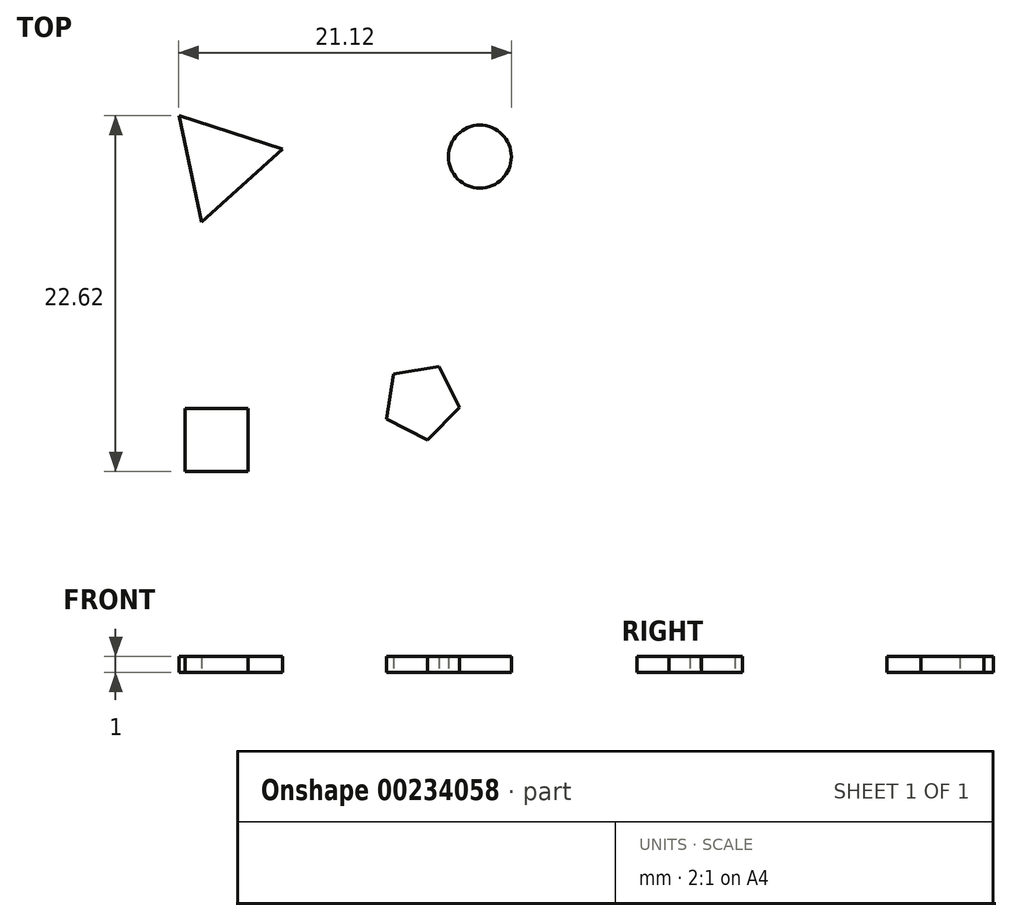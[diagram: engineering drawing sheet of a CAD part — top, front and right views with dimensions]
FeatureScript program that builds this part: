
annotation { "Feature Type Name" : "Feature", "Feature Type Description" : "" }
export const myFeature = defineFeature(function(context is Context, id is Id, definition is map)
    precondition{}
    {
        {
            var Q0;
            Q0=qCreatedBy(makeId("Top.planeOp"),FACE);
            var sketch = newSketch(context, id + "F0", { "sketchPlane" : qUnion([Q0])});
            skCircle(sketch, "E0.cCircle", {"center": v(-33.23, 10.22) * mm, "radius": 2 * mm, "construction": true});
            skLineSegment(sketch, "E0.0", {"start": v(-29.32, 11.06) * mm, "end": v(-34.46, 6.41) * mm});
            skLineSegment(sketch, "E0.1", {"start": v(-34.46, 6.41) * mm, "end": v(-35.92, 13.19) * mm});
            skLineSegment(sketch, "E0.2", {"start": v(-35.92, 13.19) * mm, "end": v(-29.32, 11.06) * mm});
            skPoint(sketch, "E0.0.midPoint", {"position": v(-31.9, 8.74) * mm});
            skCircle(sketch, "E1.cCircle", {"center": v(-33.51, -7.43) * mm, "radius": 2 * mm, "construction": true});
            skLineSegment(sketch, "E1.0", {"start": v(-31.51, -5.43) * mm, "end": v(-31.51, -9.43) * mm});
            skLineSegment(sketch, "E1.1", {"start": v(-31.51, -9.43) * mm, "end": v(-35.51, -9.43) * mm});
            skLineSegment(sketch, "E1.2", {"start": v(-35.51, -9.43) * mm, "end": v(-35.51, -5.43) * mm});
            skLineSegment(sketch, "E1.3", {"start": v(-35.51, -5.43) * mm, "end": v(-31.51, -5.43) * mm});
            skPoint(sketch, "E1.0.midPoint", {"position": v(-31.51, -7.43) * mm});
            skCircle(sketch, "E2.cCircle", {"center": v(-20.52, -4.96) * mm, "radius": 2 * mm, "construction": true});
            skLineSegment(sketch, "E2.0", {"start": v(-18.08, -5.35) * mm, "end": v(-20.13, -7.4) * mm});
            skLineSegment(sketch, "E2.1", {"start": v(-20.13, -7.4) * mm, "end": v(-22.72, -6.08) * mm});
            skLineSegment(sketch, "E2.2", {"start": v(-22.72, -6.08) * mm, "end": v(-22.27, -3.21) * mm});
            skLineSegment(sketch, "E2.3", {"start": v(-22.27, -3.21) * mm, "end": v(-19.4, -2.76) * mm});
            skLineSegment(sketch, "E2.4", {"start": v(-19.4, -2.76) * mm, "end": v(-18.08, -5.35) * mm});
            skPoint(sketch, "E2.0.midPoint", {"position": v(-19.1, -6.38) * mm});
            skCircle(sketch, "E3", {"center": v(-16.8, 10.58) * mm, "radius": 2 * mm});
            skSolve(sketch);
        }
        {
            var Q0;
            Q0=makeQuery(id+"F0.imprint","IMPRINT",FACE,{"disambiguationData":[TD([[makeQuery(id+"F0.imprint","IMPRINT",EDGE,{"derivedFrom":sQuery(id+"F0.wireOp",EDGE,"E0.0")}),-1.0]])]});
            var Q1;
            Q1=makeQuery(id+"F0.imprint","IMPRINT",FACE,{"disambiguationData":[TD([[makeQuery(id+"F0.imprint","IMPRINT",EDGE,{"derivedFrom":sQuery(id+"F0.wireOp",EDGE,"E1.0")}),-1.0]])]});
            var Q2;
            Q2=makeQuery(id+"F0.imprint","IMPRINT",FACE,{"disambiguationData":[TD([[makeQuery(id+"F0.imprint","IMPRINT",EDGE,{"derivedFrom":sQuery(id+"F0.wireOp",EDGE,"E2.0")}),-1.0]])]});
            var Q3;
            Q3=makeQuery(id+"F0.imprint","IMPRINT",FACE,{"disambiguationData":[TD([[makeQuery(id+"F0.imprint","IMPRINT",EDGE,{"derivedFrom":sQuery(id+"F0.wireOp",EDGE,"E3")}),1.0]])]});
            extrude(context, id + "F1", {"entities" : qUnion([Q0, Q1, Q2, Q3]), "depth" : 1 * mm});
        }
    });
